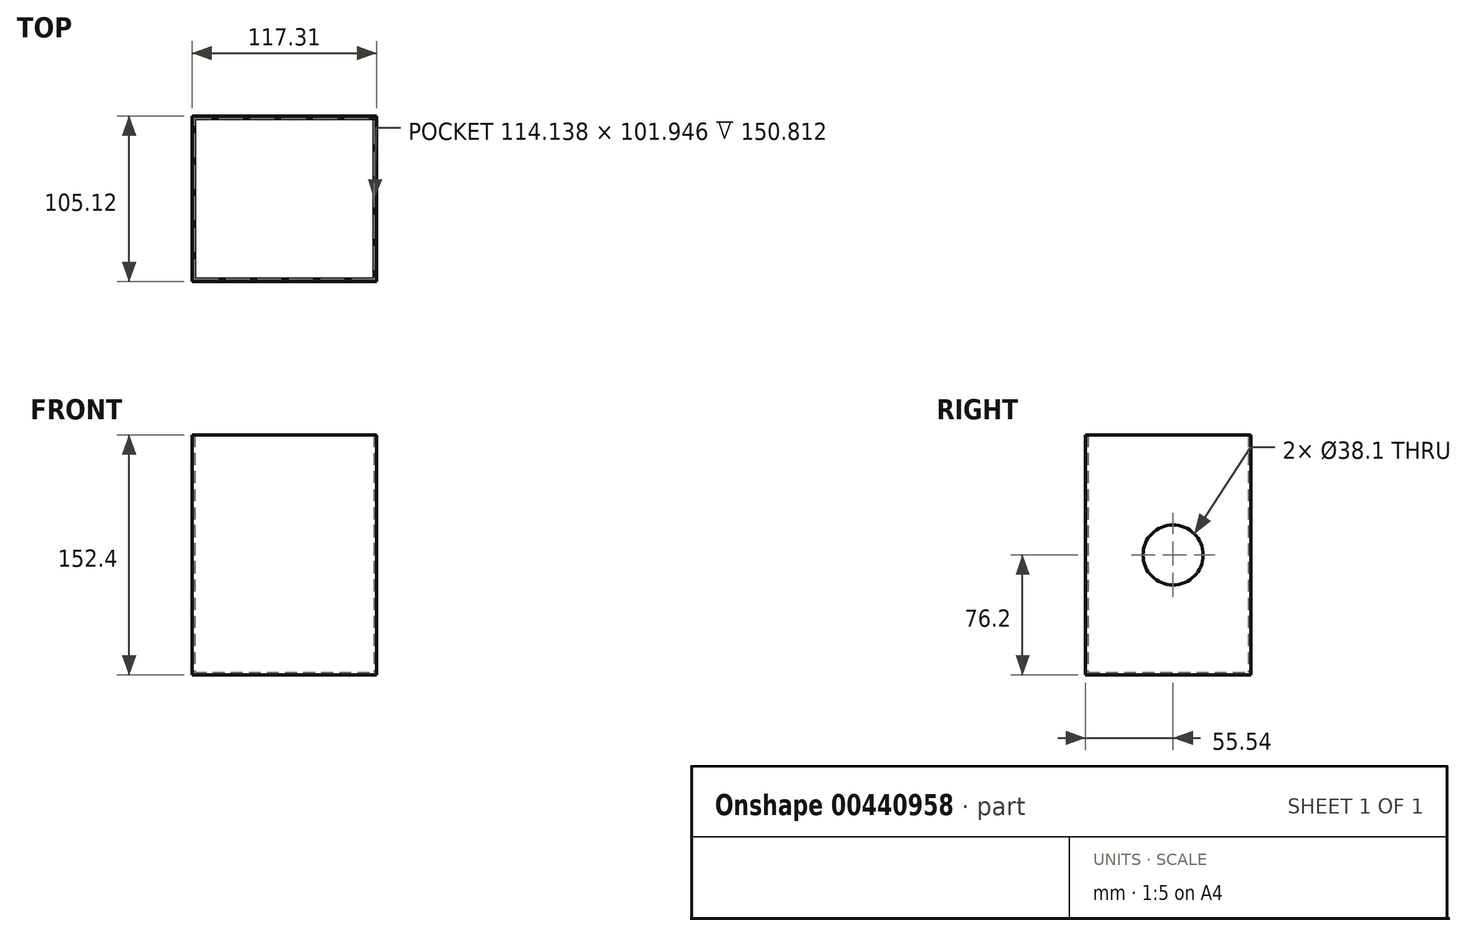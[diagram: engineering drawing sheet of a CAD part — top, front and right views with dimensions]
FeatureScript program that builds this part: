
annotation { "Feature Type Name" : "Feature", "Feature Type Description" : "" }
export const myFeature = defineFeature(function(context is Context, id is Id, definition is map)
    precondition{}
    {
        {
            var Q0;
            Q0=qCreatedBy(makeId("Top.planeOp"),FACE);
            var sketch = newSketch(context, id + "F0", { "sketchPlane" : qUnion([Q0])});
            skLineSegment(sketch, "E0.bottom", {"start": v(-68.34, -55.54) * mm, "end": v(48.97, -55.54) * mm});
            skLineSegment(sketch, "E0.top", {"start": v(-68.34, 49.58) * mm, "end": v(48.97, 49.58) * mm});
            skLineSegment(sketch, "E0.left", {"start": v(-68.34, -55.54) * mm, "end": v(-68.34, 49.58) * mm});
            skLineSegment(sketch, "E0.right", {"start": v(48.97, -55.54) * mm, "end": v(48.97, 49.58) * mm});
            skSolve(sketch);
        }
        {
            var Q0;
            Q0=makeQuery(id+"F0.imprint","IMPRINT",FACE,{"disambiguationData":[TD([[makeQuery(id+"F0.imprint","IMPRINT",EDGE,{"derivedFrom":sQuery(id+"F0.wireOp",EDGE,"E0.bottom")}),1.0]])]});
            extrude(context, id + "F1", {"entities" : qUnion([Q0]), "depth" : 152.4 * mm});
        }
        {
            var Q0;
            Q0=makeQuery(id+"F1.opExtrude","CAP_FACE",FACE,{"disambiguationData":[OSD([sQuery(id+"F0.wireOp",EDGE,"E0.bottom"),sQuery(id+"F0.wireOp",EDGE,"E0.top"),sQuery(id+"F0.wireOp",EDGE,"E0.left"),sQuery(id+"F0.wireOp",EDGE,"E0.right")])],"isStart":false});
            shell(context, id + "F2", {"entities" : qUnion([Q0]), "thickness" : 1.59 * mm});
        }
        {
            var Q0;
            Q0=makeQuery(id+"F1.opExtrude","SWEPT_FACE",FACE,{"disambiguationData":[OSD([sQuery(id+"F0.wireOp",EDGE,"E0.right")])]});
            var sketch = newSketch(context, id + "F3", { "sketchPlane" : qUnion([Q0])});
            skCircle(sketch, "E1", {"center": v(0, 76.2) * mm, "radius": 20.56 * mm});
            skPoint(sketch, "E1.centerSnap0", {"position": v(49.58, 76.2) * mm});
            skSolve(sketch);
        }
        {
            var Q0;
            Q0=sQuery(id+"F3.wireOp",VERTEX,"E1.center");
            var Q1;
            Q1=makeQuery(id+"F1.opExtrude","SWEPT_BODY",BODY,{"disambiguationData":[OSD([sQuery(id+"F0.wireOp",EDGE,"E0.bottom"),sQuery(id+"F0.wireOp",EDGE,"E0.top"),sQuery(id+"F0.wireOp",EDGE,"E0.left"),sQuery(id+"F0.wireOp",EDGE,"E0.right")])]});
            hole(context, id + "F4", {"style" : HoleStyle.SIMPLE, "endStyle" : HoleEndStyle.THROUGH, "holeDiameter" : 38.1 * mm, "isTappedThrough" : true, "tappedDepth" : 12.7 * mm, "tapClearance" : 3, "locations" : qUnion([Q0]), "scope" : qUnion([Q1])});
        }
    });
